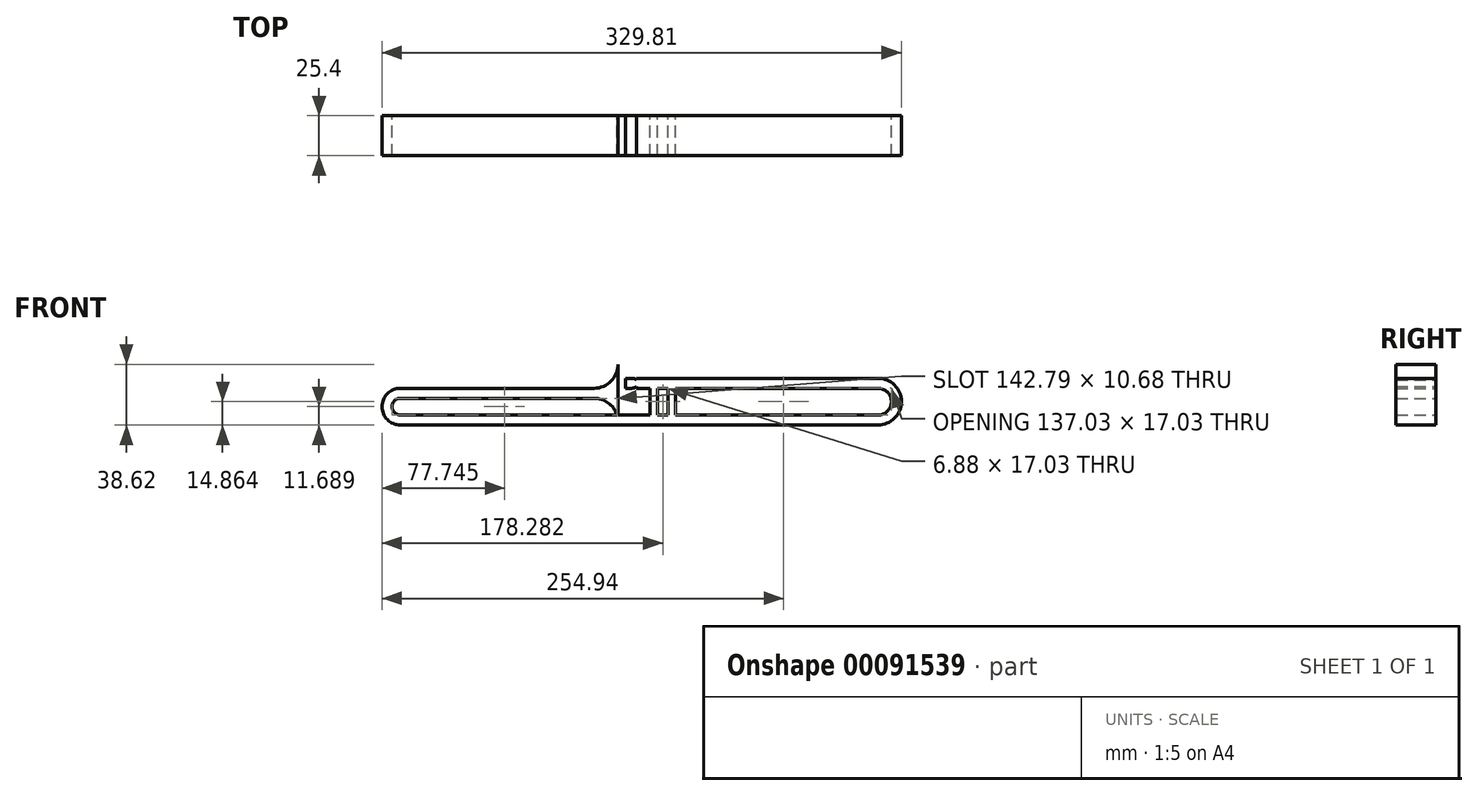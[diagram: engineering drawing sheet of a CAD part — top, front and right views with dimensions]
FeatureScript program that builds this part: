
annotation { "Feature Type Name" : "Feature", "Feature Type Description" : "" }
export const myFeature = defineFeature(function(context is Context, id is Id, definition is map)
    precondition{}
    {
        {
            var Q0;
            Q0=qCreatedBy(makeId("Front.planeOp"),FACE);
            var sketch = newSketch(context, id + "F0", { "sketchPlane" : qUnion([Q0])});
            skLineSegment(sketch, "E0.left", {"start": v(0, 0) * mm, "end": v(0, 6.35) * mm});
            skArc(sketch, "E1", {"start": v(165.1, -17.03) * mm, "mid": v(173.62, -8.52) * mm, "end": v(165.1, 0) * mm});
            skLineSegment(sketch, "E2", {"start": v(165.1, -17.03) * mm, "end": v(165.1, -23.38) * mm});
            skArc(sketch, "E3", {"start": v(165.1, -23.38) * mm, "mid": v(179.97, -8.52) * mm, "end": v(165.1, 6.35) * mm});
            skLineSegment(sketch, "E4", {"start": v(0, -23.38) * mm, "end": v(165.1, -23.38) * mm});
            skLineSegment(sketch, "E5.left", {"start": v(0, 0) * mm, "end": v(0, -17.03) * mm});
            skLineSegment(sketch, "E6", {"start": v(20.3, 0) * mm, "end": v(20.3, -17.03) * mm});
            skLineSegment(sketch, "E7", {"start": v(25, -17.03) * mm, "end": v(25, 0) * mm});
            skLineSegment(sketch, "E8.left", {"start": v(0, 6.35) * mm, "end": v(0, 0) * mm});
            skLineSegment(sketch, "E9.top", {"start": v(0, -23.38) * mm, "end": v(-100.8, -23.38) * mm});
            skLineSegment(sketch, "E10.bottom", {"start": v(-100.8, -23.38) * mm, "end": v(-138.15, -23.38) * mm});
            skLineSegment(sketch, "E10.top", {"start": v(-100.8, -17.03) * mm, "end": v(-138.15, -17.03) * mm});
            skArc(sketch, "E11", {"start": v(-138.15, -6.35) * mm, "mid": v(-143.5, -11.7) * mm, "end": v(-138.15, -17.03) * mm});
            skArc(sketch, "E12", {"start": v(-138.15, 0) * mm, "mid": v(-149.84, -11.7) * mm, "end": v(-138.15, -23.38) * mm});
            skLineSegment(sketch, "E13.right", {"start": v(0, 0) * mm, "end": v(0, -6.35) * mm});
            skLineSegment(sketch, "E14", {"start": v(0, -6.35) * mm, "end": v(0, -21.59) * mm});
            skLineSegment(sketch, "E15", {"start": v(0, -6.35) * mm, "end": v(0, 15.24) * mm});
            skLineSegment(sketch, "E16.left", {"start": v(0, 15.24) * mm, "end": v(0, -6.35) * mm});
            skLineSegment(sketch, "E17", {"start": v(-138.15, 0) * mm, "end": v(-15.24, 0) * mm});
            skArc(sketch, "E18", {"start": v(-15.24, 0) * mm, "mid": v(-4.46, 4.46) * mm, "end": v(0, 15.24) * mm});
            skArc(sketch, "E19", {"start": v(0, -21.59) * mm, "mid": v(-4.46, -10.81) * mm, "end": v(-15.24, -6.35) * mm});
            skLineSegment(sketch, "E20", {"start": v(-15.24, -6.35) * mm, "end": v(-138.15, -6.35) * mm});
            skLineSegment(sketch, "E21", {"start": v(-100.8, -17.03) * mm, "end": v(-0.7, -17.03) * mm});
            skLineSegment(sketch, "E22", {"start": v(0, -17.03) * mm, "end": v(20.3, -17.03) * mm});
            skLineSegment(sketch, "E23", {"start": v(25, -17.03) * mm, "end": v(31.88, -17.03) * mm});
            skLineSegment(sketch, "E24", {"start": v(31.88, -17.03) * mm, "end": v(31.88, 0) * mm});
            skLineSegment(sketch, "E25", {"start": v(36.58, 0) * mm, "end": v(36.58, -17.03) * mm});
            skLineSegment(sketch, "E26", {"start": v(25, 0) * mm, "end": v(31.88, 0) * mm});
            skLineSegment(sketch, "E27", {"start": v(36.58, 0) * mm, "end": v(165.1, 0) * mm});
            skLineSegment(sketch, "E28", {"start": v(165.1, -17.03) * mm, "end": v(36.58, -17.03) * mm});
            skLineSegment(sketch, "E29", {"start": v(4.7, 0) * mm, "end": v(4.7, 6.35) * mm});
            skLineSegment(sketch, "E30", {"start": v(4.7, 6.35) * mm, "end": v(8.96, 6.35) * mm});
            skLineSegment(sketch, "E31", {"start": v(12.47, 0) * mm, "end": v(20.3, 0) * mm});
            skLineSegment(sketch, "E32", {"start": v(12.47, 6.35) * mm, "end": v(165.1, 6.35) * mm});
            skLineSegment(sketch, "E33", {"start": v(4.7, 0) * mm, "end": v(8.96, 0) * mm});
            skLineSegment(sketch, "E34", {"start": v(12.47, 6.35) * mm, "end": v(11.64, 6.35) * mm});
            skLineSegment(sketch, "E35", {"start": v(11.64, 6.35) * mm, "end": v(11.64, 0) * mm});
            skLineSegment(sketch, "E36", {"start": v(11.64, 0) * mm, "end": v(12.47, 0) * mm});
            skLineSegment(sketch, "E37", {"start": v(11.64, 6.35) * mm, "end": v(11.64, 5.32) * mm});
            skLineSegment(sketch, "E38", {"start": v(11.64, 5.32) * mm, "end": v(11.64, 1.03) * mm});
            skLineSegment(sketch, "E39", {"start": v(11.64, 1.03) * mm, "end": v(11.64, 0) * mm});
            skArc(sketch, "E40", {"start": v(11.64, 5.32) * mm, "mid": v(10.4, 6.08) * mm, "end": v(8.96, 6.35) * mm});
            skArc(sketch, "E41", {"start": v(8.96, 0) * mm, "mid": v(10.4, 0.27) * mm, "end": v(11.64, 1.03) * mm});
            skSolve(sketch);
        }
        {
            var Q0;
            Q0 = qSketchRegion(id + "F0", true);
            extrude(context, id + "F1", {"entities" : qUnion([Q0]), "depth" : 25.4 * mm});
        }
    });
